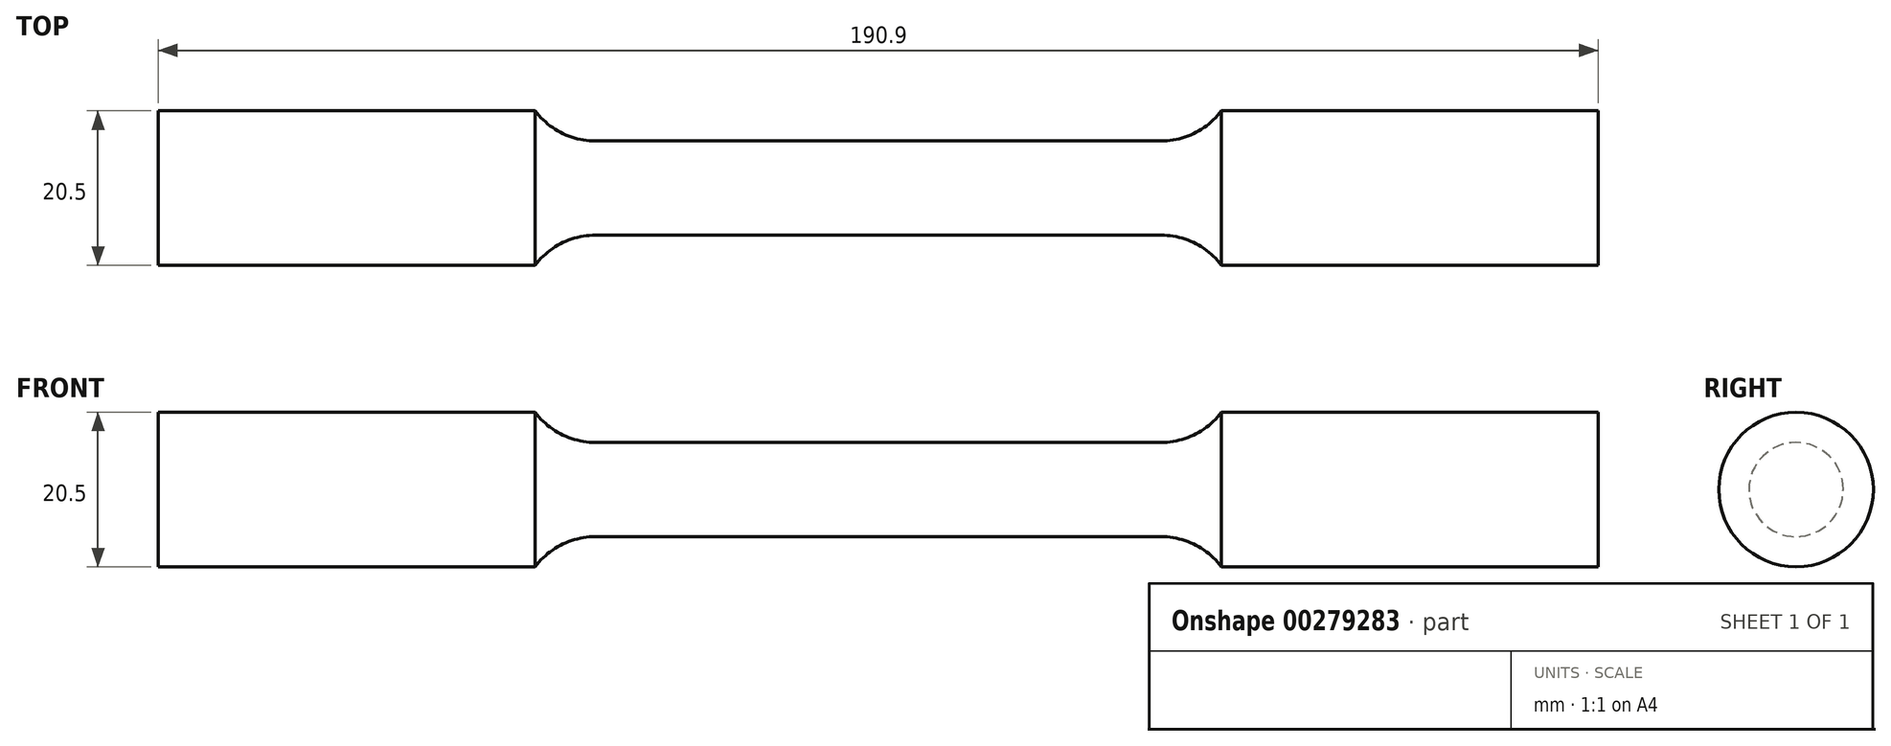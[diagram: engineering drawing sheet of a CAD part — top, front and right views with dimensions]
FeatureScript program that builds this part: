
annotation { "Feature Type Name" : "Feature", "Feature Type Description" : "" }
export const myFeature = defineFeature(function(context is Context, id is Id, definition is map)
    precondition{}
    {
        {
            var Q0;
            Q0=qCreatedBy(makeId("Front.planeOp"),FACE);
            var sketch = newSketch(context, id + "F0", { "sketchPlane" : qUnion([Q0])});
            skLineSegment(sketch, "E0", {"start": v(0, 6.25) * mm, "end": v(37.5, 6.25) * mm});
            skArc(sketch, "E1", {"start": v(37.5, 6.25) * mm, "mid": v(41.97, 7.3) * mm, "end": v(45.5, 10.25) * mm});
            skLineSegment(sketch, "E2", {"start": v(45.5, 10.25) * mm, "end": v(95.45, 10.25) * mm});
            skLineSegment(sketch, "E3", {"start": v(95.45, 0) * mm, "end": v(95.45, 10.25) * mm});
            skLineSegment(sketch, "E4.MirrorCS", {"start": v(0, 6.25) * mm, "end": v(-37.5, 6.25) * mm});
            skLineSegment(sketch, "E5.MirrorCS", {"start": v(-95.45, 0) * mm, "end": v(-95.45, 10.25) * mm});
            skLineSegment(sketch, "E6.MirrorCS", {"start": v(-45.5, 10.25) * mm, "end": v(-95.45, 10.25) * mm});
            skArc(sketch, "E7.MirrorCS", {"start": v(-37.5, 6.25) * mm, "mid": v(-41.97, 7.3) * mm, "end": v(-45.5, 10.25) * mm});
            skLineSegment(sketch, "E8", {"start": v(-95.45, 0) * mm, "end": v(95.45, 0) * mm});
            skSolve(sketch);
        }
        {
            var Q0;
            Q0 = qSketchRegion(id + "F0", true);
            var Q1;
            Q1=sQuery(id+"F0.wireOp",EDGE,"E8");
            revolve(context, id + "F1", {"entities" : qUnion([Q0]), "axis" : qUnion([Q1]), "revolveType" : RevolveType.FULL});
        }
    });
